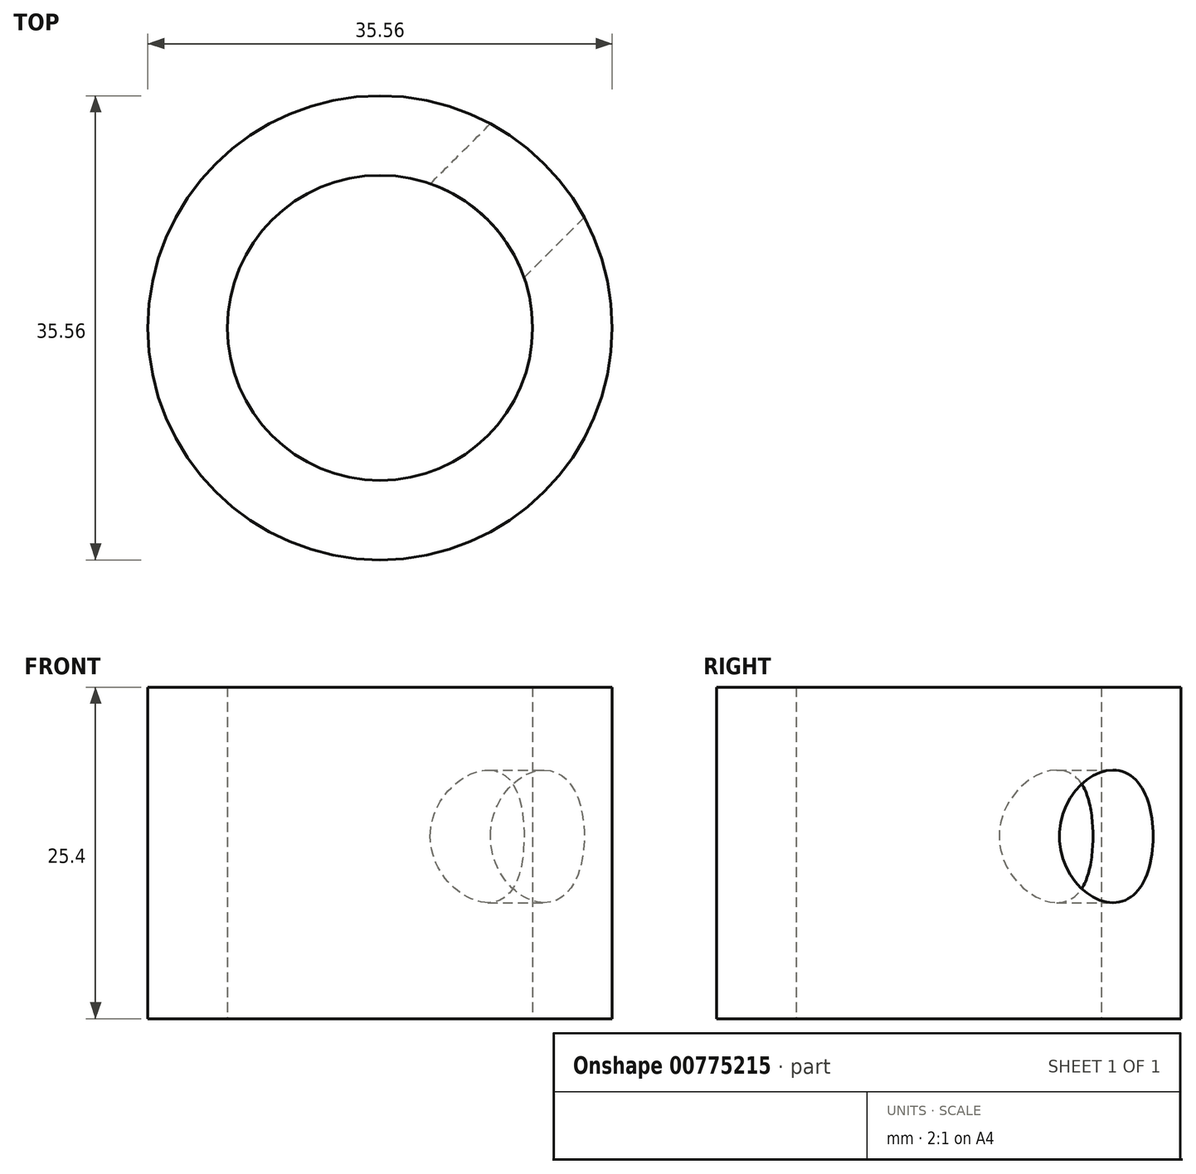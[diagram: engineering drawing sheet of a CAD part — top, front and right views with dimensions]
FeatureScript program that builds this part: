
annotation { "Feature Type Name" : "Feature", "Feature Type Description" : "" }
export const myFeature = defineFeature(function(context is Context, id is Id, definition is map)
    precondition{}
    {
        {
            var Q0;
            Q0=qCreatedBy(makeId("Top.planeOp"),FACE);
            var sketch = newSketch(context, id + "F0", { "sketchPlane" : qUnion([Q0])});
            skCircle(sketch, "E0", {"center": v(0, 0) * mm, "radius": 11.68 * mm});
            skCircle(sketch, "E1", {"center": v(0, 0) * mm, "radius": 17.78 * mm});
            skSolve(sketch);
        }
        {
            var Q0;
            Q0 = qSketchRegion(id + "F0", true);
            extrude(context, id + "F1", {"entities" : qUnion([Q0]), "depth" : 25.4 * mm, "offsetDistance" : 25.4 * mm});
        }
        {
            var Q0;
            Q0=qCreatedBy(makeId("Right.planeOp"),FACE);
            cPlane(context, id + "F2", {"entities" : qUnion([Q0]), "cplaneType" : CPlaneType.OFFSET, "offset" : 17.78 * mm, "width" : 152.4 * mm, "height" : 152.4 * mm});
        }
        {
            var Q0;
            Q0=qCreatedBy(id+"F2.planeOp",FACE);
            var sketch = newSketch(context, id + "F3", { "sketchPlane" : qUnion([Q0])});
            skLineSegment(sketch, "E2", {"start": v(0, 0) * mm, "end": v(0, 25.47) * mm});
            skSolve(sketch);
        }
        {
            var Q0;
            Q0=qCreatedBy(id+"F2.planeOp",FACE);
            var Q1;
            Q1=sQuery(id+"F3.wireOp",EDGE,"E2");
            cPlane(context, id + "F4", {"entities" : qUnion([Q0, Q1]), "cplaneType" : CPlaneType.LINE_ANGLE, "offset" : 17.78 * mm, "angle" : 45 * degree, "width" : 152.4 * mm, "height" : 152.4 * mm});
        }
        {
            var Q0;
            Q0=qCreatedBy(id+"F4.planeOp",FACE);
            cPlane(context, id + "F5", {"entities" : qUnion([Q0]), "cplaneType" : CPlaneType.OFFSET, "offset" : 5.08 * mm, "oppositeDirection" : true, "width" : 152.4 * mm, "height" : 152.4 * mm});
        }
        {
            var Q0;
            Q0=qCreatedBy(id+"F5.planeOp",FACE);
            var sketch = newSketch(context, id + "F6", { "sketchPlane" : qUnion([Q0])});
            skLineSegment(sketch, "E3", {"start": v(0, 0) * mm, "end": v(0, 20.36) * mm, "construction": true});
            skLineSegment(sketch, "E4", {"start": v(10.18, 13.97) * mm, "end": v(-18.2, 13.97) * mm, "construction": true});
            skPoint(sketch, "E5", {"position": v(0, 13.97) * mm});
            skCircle(sketch, "E6", {"center": v(0, 13.97) * mm, "radius": 5.08 * mm});
            skSolve(sketch);
        }
        {
            var Q0;
            Q0=makeQuery(id+"F6.imprint","IMPRINT",FACE,{"disambiguationData":[TD([[makeQuery(id+"F6.imprint","IMPRINT",EDGE,{"derivedFrom":sQuery(id+"F6.wireOp",EDGE,"E6")}),1.0]])]});
            extrude(context, id + "F7", {"entities" : qUnion([Q0]), "operationType" : NewBodyOperationType.REMOVE, "endBound" : BoundingType.SYMMETRIC, "depth" : 25.4 * mm, "offsetDistance" : 25.4 * mm});
        }
    });
